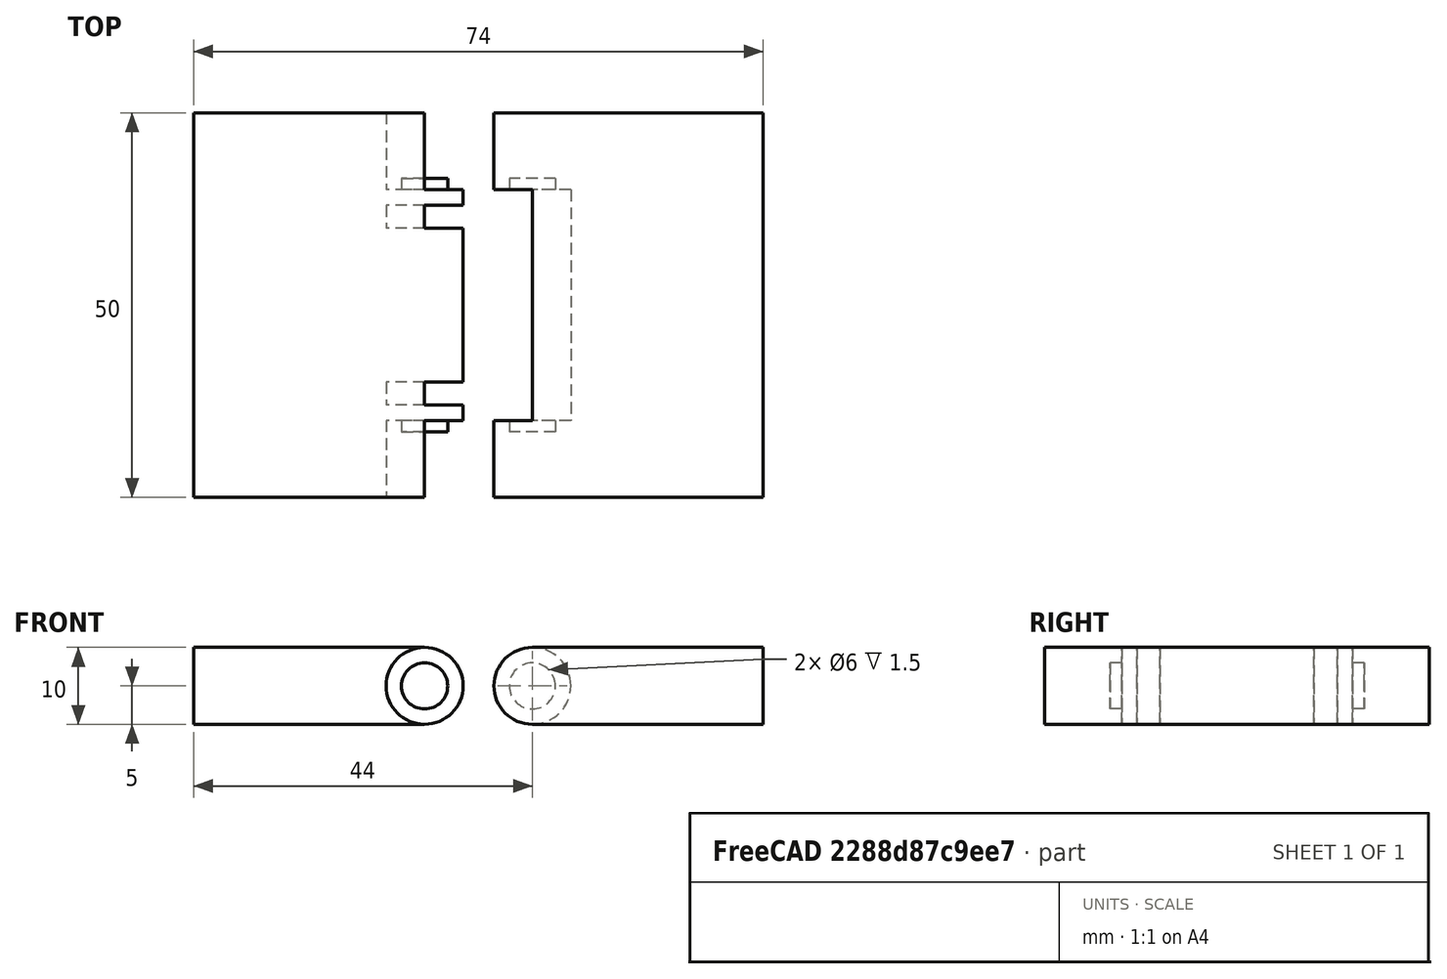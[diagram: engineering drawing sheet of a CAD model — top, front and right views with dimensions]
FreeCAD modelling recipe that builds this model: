
FCSTD DOCUMENT  (FreeCAD 0.16R6712 (Git))
Label: Hinge02
License: All rights reserved
LicenseURL: http://en.wikipedia.org/wiki/All_rights_reserved
objects: Part::Cylinder×10, Part::Cut×7, Part::Fuse×2, Part::Box×1, Part::Mirroring×1, Part::MultiFuse×1
note: 22 computed .brp shape members not serialized (recipe doc carries the construction recipe); baked Part::Feature solids carry a one-line shape summary decoded from their .brp

FEATURE [Part::Box] Box  label="Cube"
  Height = 10
  Length = 30
  Width = 50
FEATURE [Part::Cylinder] Cylinder
  Angle = 360
  Height = 50
  Placement = pos=(30,50,5) rot=(1,0,0;1.5708rad)
  Radius = 5
FEATURE [Part::Fuse] Fusion
  Base = -> Box
  Tool = -> Cylinder
FEATURE [Part::Mirroring] Part__Mirroring  label="Fusion (Mirror #1)"
  Base = (0,0,0)
  Normal = (1,0,0)
  Placement = pos=(74,0,0) rot=(0,0,1;0rad)
  Source = -> Fusion
FEATURE [Part::Cylinder] Cylinder001
  Angle = 360
  Height = 10
  Placement = pos=(30,10,5) rot=(1,0,0;1.5708rad)
  Radius = 5
FEATURE [Part::Cut] Cut
  Base = -> Fusion
  Tool = -> Cylinder001
FEATURE [Part::Cylinder] Cylinder002
  Angle = 360
  Height = 10
  Placement = pos=(30,50,5) rot=(1,0,0;1.5708rad)
  Radius = 5
FEATURE [Part::Cut] Cut001
  Base = -> Cut
  Tool = -> Cylinder002
FEATURE [Part::Cylinder] Cylinder003
  Angle = 360
  Height = 30
  Placement = pos=(44,40,5) rot=(1,0,0;1.5708rad)
  Radius = 5
FEATURE [Part::Cut] Cut002
  Base = -> Part__Mirroring
  Tool = -> Cylinder003
FEATURE [Part::Cylinder] Cylinder004
  Angle = 360
  Height = 1.5
  Placement = pos=(30,10,5) rot=(1,0,0;1.5708rad)
  Radius = 3
FEATURE [Part::Cylinder] Cylinder005
  Angle = 360
  Height = 1.5
  Placement = pos=(30,41.5,5) rot=(1,0,0;1.5708rad)
  Radius = 3
FEATURE [Part::Fuse] Fusion001
  Base = -> Cut001
  Tool = -> Cylinder005
FEATURE [Part::MultiFuse] Fusion002
  Shapes = -> [Fusion001,Cylinder004]
FEATURE [Part::Cylinder] Cylinder006
  Angle = 360
  Height = 1.5
  Placement = pos=(44,10,5) rot=(1,0,0;1.5708rad)
  Radius = 3
FEATURE [Part::Cylinder] Cylinder007
  Angle = 360
  Height = 1.5
  Placement = pos=(44,41.5,5) rot=(1,0,0;1.5708rad)
  Radius = 3
FEATURE [Part::Cut] Cut003
  Base = -> Cut002
  Tool = -> Cylinder006
FEATURE [Part::Cut] Cut004
  Base = -> Cut003
  Tool = -> Cylinder007
FEATURE [Part::Cylinder] Cylinder008
  Angle = 360
  Height = 3
  Placement = pos=(30,15,5) rot=(1,0,0;1.5708rad)
  Radius = 5
FEATURE [Part::Cylinder] Cylinder009
  Angle = 360
  Height = 3
  Placement = pos=(30,38,5) rot=(1,0,0;1.5708rad)
  Radius = 5
FEATURE [Part::Cut] Cut005
  Base = -> Fusion002
  Tool = -> Cylinder008
FEATURE [Part::Cut] Cut006
  Base = -> Cut005
  Tool = -> Cylinder009
